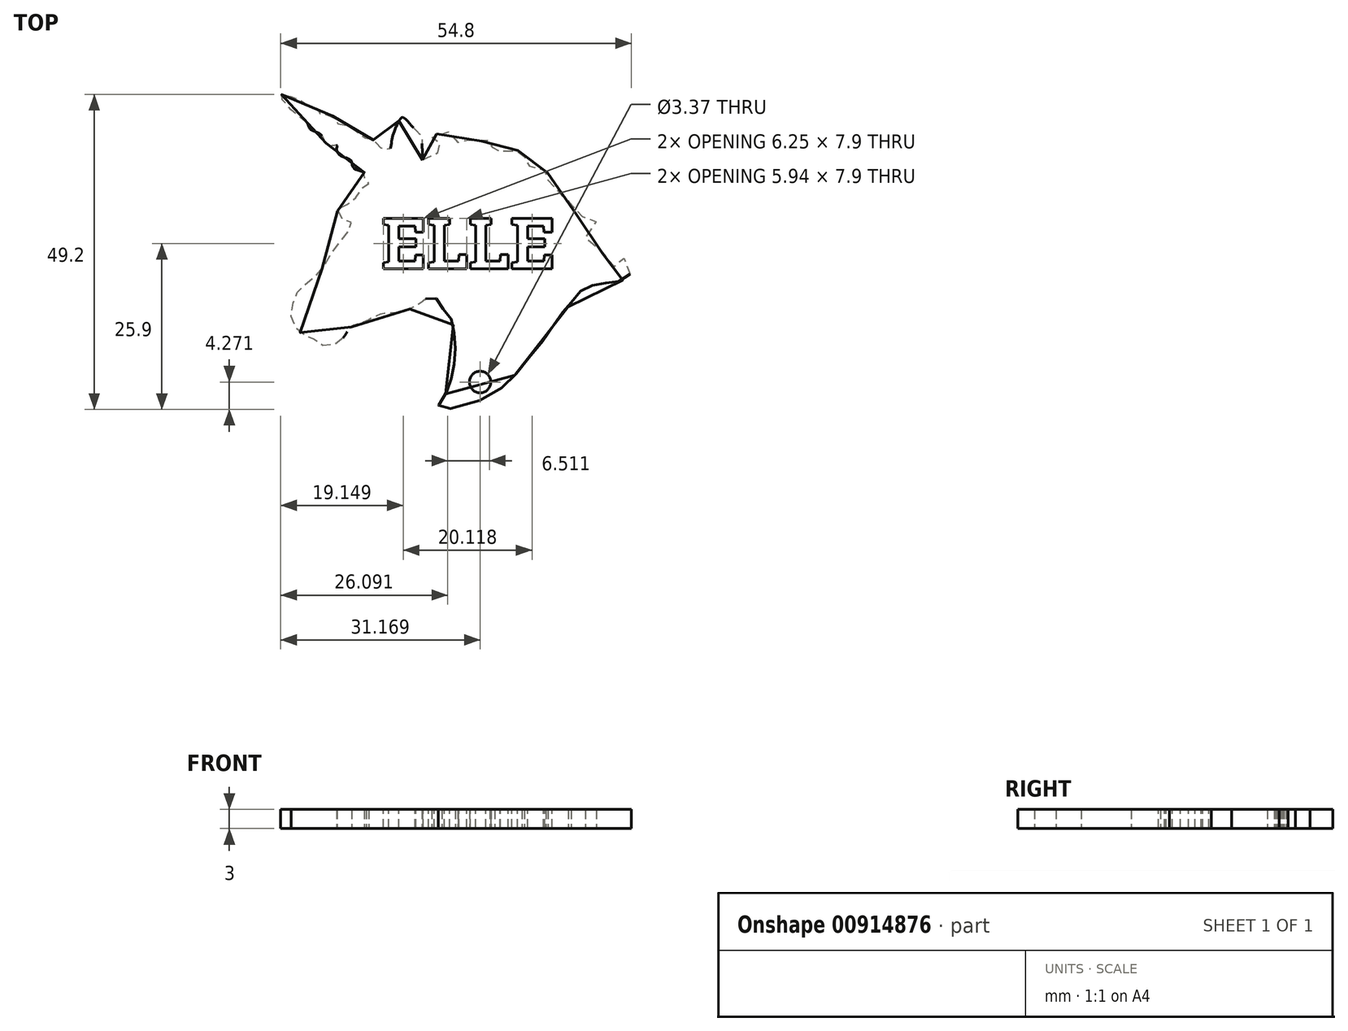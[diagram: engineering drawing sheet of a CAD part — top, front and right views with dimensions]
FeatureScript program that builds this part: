
annotation { "Feature Type Name" : "Feature", "Feature Type Description" : "" }
export const myFeature = defineFeature(function(context is Context, id is Id, definition is map)
    precondition{}
    {
        {
            var Q0;
            Q0=qCreatedBy(makeId("Top.planeOp"),FACE);
            var sketch = newSketch(context, id + "F0", { "sketchPlane" : qUnion([Q0])});
            skFitSpline(sketch, "E0", {"points": [v(28.31, 46.46) * mm, v(29.78, 47.5) * mm, v(31, 47.67) * mm, v(31.34, 48.7) * mm, v(31, 49.05) * mm, v(30.04, 48.88) * mm, v(29.78, 49.83) * mm, v(31, 50.7) * mm, v(32.8, 50.78) * mm, v(33.85, 49.83) * mm, v(33.85, 48.97) * mm, v(34.63, 49.49) * mm, v(36.27, 49.49) * mm, v(38.26, 49.49) * mm, v(39.56, 49.66) * mm, v(39.13, 48.36) * mm, v(38.87, 47.84) * mm, v(40.25, 47.84) * mm, v(41.8, 47.76) * mm, v(43.45, 48.02) * mm, v(43.89, 48.28) * mm, v(44.15, 46.37) * mm, v(43.89, 45.68) * mm, v(45.79, 45.42) * mm, v(46.74, 44.9) * mm, v(47.87, 44.73) * mm, v(47.6, 43.69) * mm, v(48.82, 42.65) * mm, v(50.2, 40.92) * mm, v(51.5, 40.83) * mm, v(51.07, 39.02) * mm, v(53.5, 37.63) * mm, v(54.96, 37.63) * mm, v(55.3, 35.99) * mm, v(53.75, 34.34) * mm, v(55.3, 33.22) * mm, v(56.95, 30.97) * mm, v(58.5, 29.76) * mm, v(59.63, 30.54) * mm, v(59.8, 31.14) * mm, v(60.93, 29.41) * mm, v(59.8, 27.77) * mm, v(57.9, 27.34) * mm, v(56, 27.08) * mm, v(54.1, 26.64) * mm, v(52.45, 25.43) * mm, v(51.07, 23.53) * mm, v(49.86, 22.32) * mm, v(48.21, 19.63) * mm, v(45.1, 15.74) * mm, v(42.24, 12.28) * mm, v(37.3, 8.9) * mm, v(30.82, 7.7) * mm, v(31.68, 9.51) * mm, v(32.64, 11.76) * mm, v(33.07, 13.66) * mm, v(33.42, 16.43) * mm, v(33.24, 19.03) * mm, v(32.9, 21.37) * mm, v(31.77, 22.84) * mm, v(30.82, 24.4) * mm, v(29.7, 25.17) * mm, v(28.05, 24.13) * mm, v(25.8, 23) * mm, v(23.81, 22.58) * mm, v(21.73, 22.32) * mm, v(19.66, 21.37) * mm, v(18.27, 20.85) * mm, v(17.23, 20.41) * mm, v(16.28, 19.2) * mm, v(15.07, 17.9) * mm, v(12.65, 17.47) * mm, v(10.83, 18.77) * mm, v(9.45, 19.29) * mm, v(7.8, 21.88) * mm, v(8.4, 25) * mm, v(9.27, 26.47) * mm, v(11.96, 28.63) * mm, v(13.95, 31.66) * mm, v(15.94, 34.26) * mm, v(17.23, 36.6) * mm, v(15.85, 37.2) * mm, v(15.07, 38.93) * mm, v(17.32, 39.8) * mm, v(18.7, 41.96) * mm, v(19.92, 42.74) * mm, v(19.22, 43.43) * mm, v(19.48, 44.3) * mm, v(17.58, 45.16) * mm, v(17.15, 46.37) * mm, v(15.76, 46.98) * mm, v(14.9, 48.02) * mm, v(14.9, 48.7) * mm, v(13.69, 48.7) * mm, v(12.48, 50.35) * mm, v(10.75, 51.3) * mm, v(10.31, 52.17) * mm, v(8.5, 53.64) * mm, v(6.16, 56.58) * mm, v(7.89, 56.32) * mm, v(9.53, 55.63) * mm, v(10.05, 55.11) * mm, v(11.87, 54.42) * mm, v(12.39, 53.64) * mm, v(14.3, 53.3) * mm, v(14.98, 52.17) * mm, v(16.28, 51.9) * mm, v(17.4, 51.3) * mm, v(18.62, 50.44) * mm, v(19.05, 50) * mm, v(20.1, 49.75) * mm, v(21.04, 49.23) * mm, v(21.73, 48.36) * mm, v(22.69, 48.19) * mm, v(23.2, 48.19) * mm, v(23.46, 49.14) * mm, v(23.72, 50.44) * mm, v(24.5, 52.34) * mm, v(25.2, 53.12) * mm, v(26.58, 51.82) * mm, v(28.14, 50) * mm, v(28.22, 48.7) * mm, v(28.31, 47.32) * mm, v(28.31, 46.46) * mm]});
            skCircle(sketch, "E1", {"center": v(37.3, 11.76) * mm, "radius": 1.68 * mm});
            skSolve(sketch);
        }
        {
            var Q0;
            Q0=makeQuery(id+"F0.imprint","IMPRINT",FACE,{"disambiguationData":[TD([[makeQuery(id+"F0.imprint","IMPRINT",EDGE,{"derivedFrom":sQuery(id+"F0.wireOp",EDGE,"E0")}),-1.0]])]});
            extrude(context, id + "F1", {"entities" : qUnion([Q0]), "depth" : 3 * mm, "offsetDistance" : 25.4 * mm});
        }
        {
            var Q0;
            Q0=makeQuery(id+"F1.opExtrude","CAP_FACE",FACE,{"disambiguationData":[OSD([sQuery(id+"F0.wireOp",EDGE,"E0"),sQuery(id+"F0.wireOp",EDGE,"E1")])],"isStart":false});
            var sketch = newSketch(context, id + "F2", { "sketchPlane" : qUnion([Q0])});
            skText(sketch, "E2", { "text": "ELLE", "fontName": "RobotoSlab-Bold.ttf"});
            const initialGuessF2  = {"E2": [0.02186, 0.02944, 1, 0, 0.008]};
            skSetInitialGuess(sketch, initialGuessF2);
            skSolve(sketch);
        }
        {
            var Q0;
            Q0=qSketchRegion(id+"F2",true);
            extrude(context, id + "F3", {"entities" : qUnion([Q0]), "operationType" : NewBodyOperationType.REMOVE, "depth" : -5 * mm, "offsetDistance" : 25 * mm});
        }
    });
